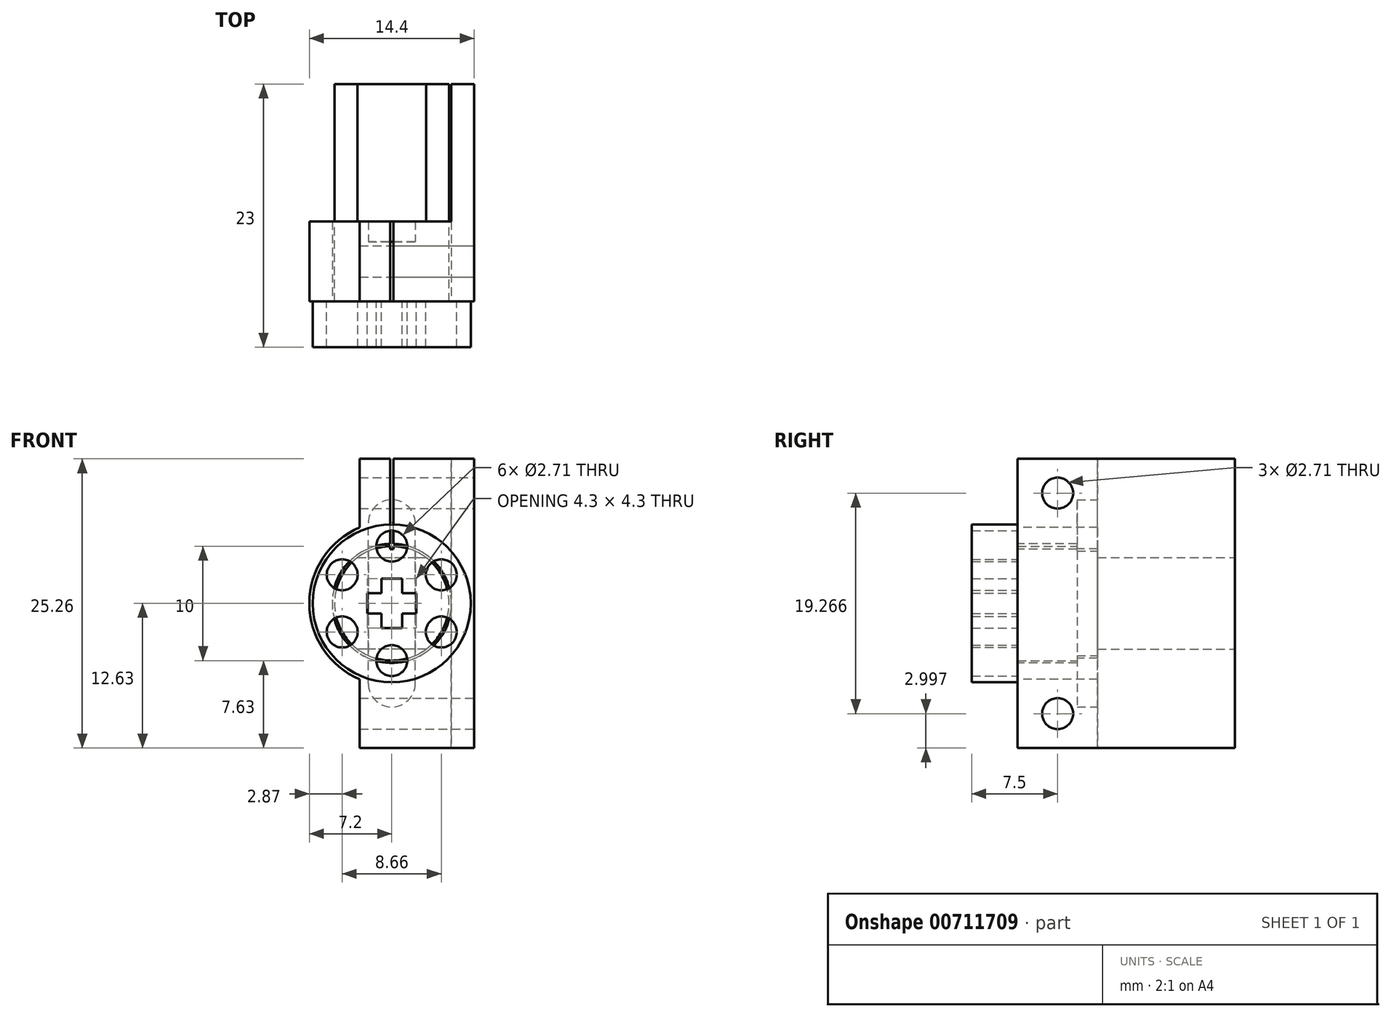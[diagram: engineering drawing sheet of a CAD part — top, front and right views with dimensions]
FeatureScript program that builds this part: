
annotation { "Feature Type Name" : "Feature", "Feature Type Description" : "" }
export const myFeature = defineFeature(function(context is Context, id is Id, definition is map)
    precondition{}
    {
        {
            var Q0;
            Q0=qCreatedBy(makeId("Front.planeOp"),FACE);
            var sketch = newSketch(context, id + "F0", { "sketchPlane" : qUnion([Q0])});
            skArc(sketch, "E0", {"start": v(-3, 4) * mm, "mid": v(-5, 0) * mm, "end": v(-3, -4) * mm});
            skLineSegment(sketch, "E1", {"start": v(-3, 4) * mm, "end": v(3, 4) * mm});
            skLineSegment(sketch, "E2", {"start": v(3, -4) * mm, "end": v(-3, -4) * mm});
            skArc(sketch, "E3.trimOffspring", {"start": v(3, -4) * mm, "mid": v(5, 0) * mm, "end": v(3, 4) * mm});
            skSolve(sketch);
        }
        {
            var Q0;
            Q0 = qSketchRegion(id + "F0", true);
            extrude(context, id + "F1", {"entities" : qUnion([Q0]), "depth" : 12 * mm, "offsetDistance" : 25.4 * mm});
        }
        {
            var Q0;
            Q0=makeQuery(id+"F1.opExtrude","CAP_FACE",FACE,{"disambiguationData":[OSD([sQuery(id+"F0.wireOp",EDGE,"E0"),sQuery(id+"F0.wireOp",EDGE,"E1"),sQuery(id+"F0.wireOp",EDGE,"E2"),sQuery(id+"F0.wireOp",EDGE,"E3.trimOffspring")])],"isStart":false});
            var sketch = newSketch(context, id + "F2", { "sketchPlane" : qUnion([Q0])});
            skCircle(sketch, "E4", {"center": v(0, 0) * mm, "radius": 5 * mm});
            skSolve(sketch);
        }
        {
            var Q0;
            Q0 = qSketchRegion(id + "F2", true);
            extrude(context, id + "F3", {"entities" : qUnion([Q0]), "operationType" : NewBodyOperationType.ADD, "depth" : 7 * mm, "offsetDistance" : 25 * mm});
        }
        {
            var Q0;
            Q0=makeQuery(id+"F3.opExtrude","CAP_FACE",FACE,{"disambiguationData":[OSD([sQuery(id+"F2.wireOp",EDGE,"E4")])],"isStart":false});
            var sketch = newSketch(context, id + "F4", { "sketchPlane" : qUnion([Q0])});
            skLineSegment(sketch, "E5.bottom", {"start": v(-0.75, 2) * mm, "end": v(0.75, 2) * mm});
            skLineSegment(sketch, "E5.top", {"start": v(-0.75, -2) * mm, "end": v(0.75, -2) * mm});
            skLineSegment(sketch, "E5.left", {"start": v(-0.75, 2) * mm, "end": v(-0.75, 0.75) * mm});
            skLineSegment(sketch, "E5.right", {"start": v(0.75, 2) * mm, "end": v(0.75, 0.75) * mm});
            skPoint(sketch, "E5.middle", {"position": v(0, 0) * mm});
            skLineSegment(sketch, "E6.bottom", {"start": v(-2, 0.75) * mm, "end": v(-0.75, 0.75) * mm});
            skLineSegment(sketch, "E6.top", {"start": v(-2, -0.75) * mm, "end": v(-0.75, -0.75) * mm});
            skLineSegment(sketch, "E6.left", {"start": v(-2, 0.75) * mm, "end": v(-2, -0.75) * mm});
            skLineSegment(sketch, "E6.right", {"start": v(2, 0.75) * mm, "end": v(2, -0.75) * mm});
            skLineSegment(sketch, "E7.trimOffspring", {"start": v(0.75, -0.75) * mm, "end": v(2, -0.75) * mm});
            skLineSegment(sketch, "E8.trimOffspring", {"start": v(-0.75, -0.75) * mm, "end": v(-0.75, -2) * mm});
            skLineSegment(sketch, "E9.trimOffspring", {"start": v(0.75, 0.75) * mm, "end": v(2, 0.75) * mm});
            skLineSegment(sketch, "E10.trimOffspring", {"start": v(0.75, -0.75) * mm, "end": v(0.75, -2) * mm});
            skSolve(sketch);
        }
        {
            var Q0;
            Q0 = qSketchRegion(id + "F4", true);
            extrude(context, id + "F5", {"entities" : qUnion([Q0]), "operationType" : NewBodyOperationType.ADD, "depth" : 2 * mm, "offsetDistance" : 25 * mm});
        }
        {
            var Q0;
            Q0=makeQuery(id+"F5.opExtrude","CAP_FACE",FACE,{"disambiguationData":[OSD([sQuery(id+"F4.wireOp",EDGE,"E5.bottom"),sQuery(id+"F4.wireOp",EDGE,"E5.top"),sQuery(id+"F4.wireOp",EDGE,"E5.left"),sQuery(id+"F4.wireOp",EDGE,"E5.right"),sQuery(id+"F4.wireOp",EDGE,"E6.bottom"),sQuery(id+"F4.wireOp",EDGE,"E6.top"),sQuery(id+"F4.wireOp",EDGE,"E6.left"),sQuery(id+"F4.wireOp",EDGE,"E6.right"),sQuery(id+"F4.wireOp",EDGE,"E7.trimOffspring"),sQuery(id+"F4.wireOp",EDGE,"E8.trimOffspring"),sQuery(id+"F4.wireOp",EDGE,"E9.trimOffspring"),sQuery(id+"F4.wireOp",EDGE,"E10.trimOffspring")])],"isStart":false});
            var sketch = newSketch(context, id + "F6", { "sketchPlane" : qUnion([Q0])});
            skCircle(sketch, "E11", {"center": v(0, 0) * mm, "radius": 0.75 * mm});
            skSolve(sketch);
        }
        {
            var Q0;
            Q0 = qSketchRegion(id + "F6", true);
            extrude(context, id + "F7", {"entities" : qUnion([Q0]), "operationType" : NewBodyOperationType.ADD, "depth" : 1 * mm, "offsetDistance" : 25 * mm});
        }
        {
            var Q0;
            {var subQ0=sQuery(id+"F2.wireOp",EDGE,"E4");Q0=makeQuery(id+"F3.boolean.opBoolean","SPLIT",FACE,{"disambiguationData":[TD([makeQuery(id+"F1.opExtrude","SWEPT_FACE",FACE,{"disambiguationData":[OSD([sQuery(id+"F0.wireOp",EDGE,"E1")])]})])],"derivedFrom":makeQuery(id+"F3.opExtrude","CAP_FACE",FACE,{"disambiguationData":[OSD([subQ0])],"isStart":true})});}
            var sketch = newSketch(context, id + "F8", { "sketchPlane" : qUnion([Q0])});
            skLineSegment(sketch, "E12", {"start": v(0, 0) * mm, "end": v(0, 7) * mm, "construction": true});
            skPoint(sketch, "E12.endSnap0", {"position": v(0, 5) * mm});
            skCircle(sketch, "E13", {"center": v(0, 7) * mm, "radius": 1 * mm});
            skLineSegment(sketch, "E14", {"start": v(-1.9, 4) * mm, "end": v(-1.9, 7) * mm});
            skArc(sketch, "E15", {"start": v(-1.9, 7) * mm, "mid": v(0, 8.9) * mm, "end": v(1.9, 7) * mm});
            skLineSegment(sketch, "E16", {"start": v(1.9, 7) * mm, "end": v(1.9, 4) * mm});
            skLineSegment(sketch, "E17", {"start": v(1.9, 4) * mm, "end": v(-1.9, 4) * mm});
            skLineSegment(sketch, "E18", {"start": v(0, 0) * mm, "end": v(-2.98, 0) * mm, "construction": true});
            skPoint(sketch, "E19.MirrorP", {"position": v(0, -5) * mm});
            skLineSegment(sketch, "E20.MirrorCS", {"start": v(0, 0) * mm, "end": v(0, -7) * mm, "construction": true});
            skCircle(sketch, "E21.MirrorC", {"center": v(0, -7) * mm, "radius": 1 * mm});
            skLineSegment(sketch, "E22.MirrorCS", {"start": v(-1.9, -4) * mm, "end": v(-1.9, -7) * mm});
            skLineSegment(sketch, "E23.MirrorCS", {"start": v(1.9, -7) * mm, "end": v(1.9, -4) * mm});
            skLineSegment(sketch, "E24.MirrorCS", {"start": v(1.9, -4) * mm, "end": v(-1.9, -4) * mm});
            skArc(sketch, "E25.MirrorCS", {"start": v(-1.9, -7) * mm, "mid": v(0, -8.9) * mm, "end": v(1.9, -7) * mm});
            skSolve(sketch);
        }
        {
            var Q0;
            Q0 = qSketchRegion(id + "F8", true);
            extrude(context, id + "F9", {"entities" : qUnion([Q0]), "operationType" : NewBodyOperationType.ADD, "oppositeDirection" : true, "depth" : 1.8 * mm, "offsetDistance" : 25 * mm});
        }
        {
            var Q0;
            Q0=makeQuery(id+"F1.opExtrude","SWEPT_BODY",BODY,{"disambiguationData":[OSD([sQuery(id+"F0.wireOp",EDGE,"E0"),sQuery(id+"F0.wireOp",EDGE,"E1"),sQuery(id+"F0.wireOp",EDGE,"E2"),sQuery(id+"F0.wireOp",EDGE,"E3.trimOffspring")])]});
            transform(context, id + "F10", {"entities" : qUnion([Q0]), "transformType" : TransformType.TRANSLATION_3D, "dx" : 0 * mm, "dy" : 0 * mm, "dz" : 0 * mm, "makeCopy" : true});
        }
        {
            var Q0;
            Q0=makeQuery(id+"F10.opPattern","COPY",BODY,{"derivedFrom":makeQuery(id+"F1.opExtrude","SWEPT_BODY",BODY,{"disambiguationData":[OSD([sQuery(id+"F0.wireOp",EDGE,"E0"),sQuery(id+"F0.wireOp",EDGE,"E1"),sQuery(id+"F0.wireOp",EDGE,"E2"),sQuery(id+"F0.wireOp",EDGE,"E3.trimOffspring")])]}),"instanceName":"1"});
            deleteBodies(context, id + "F11", {"entities" : qUnion([Q0])});
        }
        {
            var Q0;
            Q0=makeQuery(id+"F3.opExtrude","CAP_FACE",FACE,{"disambiguationData":[OSD([sQuery(id+"F2.wireOp",EDGE,"E4")])],"isStart":false});
            var sketch = newSketch(context, id + "F12", { "sketchPlane" : qUnion([Q0])});
            skCircle(sketch, "E26.0", {"center": v(0, 0) * mm, "radius": 5.2 * mm});
            skLineSegment(sketch, "E27", {"start": v(7.2, 0) * mm, "end": v(7.2, 12.63) * mm});
            skLineSegment(sketch, "E28", {"start": v(7.2, 12.63) * mm, "end": v(-2.8, 12.63) * mm});
            skLineSegment(sketch, "E29", {"start": v(-2.8, 12.63) * mm, "end": v(-2.8, 6.63) * mm});
            skArc(sketch, "E30", {"start": v(-2.8, 6.63) * mm, "mid": v(-7.2, 0) * mm, "end": v(-2.8, -6.63) * mm});
            skLineSegment(sketch, "E31", {"start": v(0, 7.2) * mm, "end": v(0, 0) * mm, "construction": true});
            skLineSegment(sketch, "E32", {"start": v(7.2, 0) * mm, "end": v(7.2, -12.63) * mm});
            skLineSegment(sketch, "E33", {"start": v(7.2, -12.63) * mm, "end": v(-2.8, -12.63) * mm});
            skLineSegment(sketch, "E34", {"start": v(-2.8, -12.63) * mm, "end": v(-2.8, -6.63) * mm});
            skSolve(sketch);
        }
        {
            var Q0;
            Q0=makeQuery(id+"F12.imprint","IMPRINT",FACE,{"disambiguationData":[TD([[makeQuery(id+"F12.imprint","IMPRINT",EDGE,{"derivedFrom":sQuery(id+"F12.wireOp",EDGE,"E26.0")}),-1.0]])]});
            var Q1;
            {var subQ0=sQuery(id+"F2.wireOp",EDGE,"E4");Q1=makeQuery(id+"F9.boolean.opBoolean","MERGE",FACE,{"derivedFrom":[makeQuery(id+"F3.boolean.opBoolean","SPLIT",FACE,{"disambiguationData":[TD([makeQuery(id+"F1.opExtrude","SWEPT_FACE",FACE,{"disambiguationData":[OSD([sQuery(id+"F0.wireOp",EDGE,"E2")])]})])],"derivedFrom":makeQuery(id+"F3.opExtrude","CAP_FACE",FACE,{"disambiguationData":[OSD([subQ0])],"isStart":true})}),makeQuery(id+"F9.opExtrude","CAP_FACE",FACE,{"disambiguationData":[OSD([sQuery(id+"F8.wireOp",EDGE,"E21.MirrorC"),sQuery(id+"F8.wireOp",EDGE,"E22.MirrorCS"),sQuery(id+"F8.wireOp",EDGE,"E23.MirrorCS"),sQuery(id+"F8.wireOp",EDGE,"E24.MirrorCS"),sQuery(id+"F8.wireOp",EDGE,"E25.MirrorCS")])],"isStart":true})]});}
            extrude(context, id + "F13", {"entities" : qUnion([Q0]), "endBound" : BoundingType.UP_TO_SURFACE, "oppositeDirection" : true, "depth" : 25 * mm, "endBoundEntityFace" : qUnion([Q1]), "offsetDistance" : 25 * mm});
        }
        {
            var Q0;
            Q0=makeQuery(id+"F13.opExtrude","CAP_FACE",FACE,{"disambiguationData":[OSD([sQuery(id+"F12.wireOp",EDGE,"E26.0"),sQuery(id+"F12.wireOp",EDGE,"E27"),sQuery(id+"F12.wireOp",EDGE,"E28"),sQuery(id+"F12.wireOp",EDGE,"E29"),sQuery(id+"F12.wireOp",EDGE,"E30"),sQuery(id+"F12.wireOp",EDGE,"E32"),sQuery(id+"F12.wireOp",EDGE,"E33"),sQuery(id+"F12.wireOp",EDGE,"E34")])],"isStart":false});
            var sketch = newSketch(context, id + "F14", { "sketchPlane" : qUnion([Q0])});
            skArc(sketch, "E35.0", {"start": v(-2.05, -7) * mm, "mid": v(0, -9.05) * mm, "end": v(2.05, -7) * mm});
            skLineSegment(sketch, "E36", {"start": v(2.05, -7) * mm, "end": v(2.05, 4.78) * mm});
            skLineSegment(sketch, "E37", {"start": v(-2.05, -7) * mm, "end": v(-2.05, 4.78) * mm});
            skLineSegment(sketch, "E38.0", {"start": v(2.05, 7) * mm, "end": v(2.05, 4.65) * mm});
            skArc(sketch, "E38.1", {"start": v(-2.05, 7) * mm, "mid": v(0, 9.05) * mm, "end": v(2.05, 7) * mm});
            skLineSegment(sketch, "E38.2", {"start": v(-2.05, 4.62) * mm, "end": v(-2.05, 7) * mm});
            skSolve(sketch);
        }
        {
            var Q0;
            Q0 = qSketchRegion(id + "F14", true);
            var Q1;
            Q1=makeQuery(id+"F9.opExtrude","CAP_FACE",FACE,{"disambiguationData":[OSD([sQuery(id+"F8.wireOp",EDGE,"E13"),sQuery(id+"F8.wireOp",EDGE,"E14"),sQuery(id+"F8.wireOp",EDGE,"E15"),sQuery(id+"F8.wireOp",EDGE,"E16"),sQuery(id+"F8.wireOp",EDGE,"E17")])],"isStart":false});
            extrude(context, id + "F15", {"entities" : qUnion([Q0]), "operationType" : NewBodyOperationType.REMOVE, "endBound" : BoundingType.UP_TO_SURFACE, "oppositeDirection" : true, "depth" : 25 * mm, "endBoundEntityFace" : qUnion([Q1]), "offsetDistance" : 25 * mm});
        }
        {
            var Q0;
            Q0=makeQuery(id+"F13.opExtrude","SWEPT_FACE",FACE,{"disambiguationData":[OSD([sQuery(id+"F12.wireOp",EDGE,"E34")])]});
            var sketch = newSketch(context, id + "F16", { "sketchPlane" : qUnion([Q0])});
            skPoint(sketch, "E39", {"position": v(15.5, -9.63) * mm});
            skPoint(sketch, "E39.positionSnap0", {"position": v(19, -9.63) * mm});
            skPoint(sketch, "E39.positionSnap1", {"position": v(15.5, -12.63) * mm});
            skPoint(sketch, "E40", {"position": v(15.5, 9.63) * mm});
            skSolve(sketch);
        }
        {
            var Q0;
            Q0=sQuery(id+"F16.wireOp",VERTEX,"E39");
            var Q1;
            Q1=sQuery(id+"F16.wireOp",VERTEX,"E40");
            var Q2;
            Q2=makeQuery(id+"F13.opExtrude","SWEPT_BODY",BODY,{"disambiguationData":[OSD([sQuery(id+"F12.wireOp",EDGE,"E26.0"),sQuery(id+"F12.wireOp",EDGE,"E27"),sQuery(id+"F12.wireOp",EDGE,"E28"),sQuery(id+"F12.wireOp",EDGE,"E29"),sQuery(id+"F12.wireOp",EDGE,"E30"),sQuery(id+"F12.wireOp",EDGE,"E32"),sQuery(id+"F12.wireOp",EDGE,"E33"),sQuery(id+"F12.wireOp",EDGE,"E34")])]});
            hole(context, id + "F17", {"style" : HoleStyle.SIMPLE, "endStyle" : HoleEndStyle.THROUGH, "standardTappedOrClearance" : lookupTablePath({ "standard" : "ANSI", "engagement" : "75%", "pitch" : "32 tpi", "size" : "#6", "type" : "Tapped" }), "standardBlindInLast" : lookupTablePath({ "fit" : "Free", "standard" : "ANSI", "engagement" : "75%", "pitch" : "32 tpi", "size" : "#6", "type" : "Clearance & tapped" }), "holeDiameter" : 2.7 * mm, "majorDiameter" : 3.5 * mm, "showTappedDepth" : true, "tappedDepth" : 5 * mm, "tapClearance" : 3, "locations" : qUnion([Q0, Q1]), "scope" : qUnion([Q2]), "startStyle" : HoleStartStyle.SKETCH});
        }
        {
            var Q0;
            Q0=makeQuery(id+"F13.opExtrude","CAP_FACE",FACE,{"disambiguationData":[OSD([sQuery(id+"F12.wireOp",EDGE,"E26.0"),sQuery(id+"F12.wireOp",EDGE,"E27"),sQuery(id+"F12.wireOp",EDGE,"E28"),sQuery(id+"F12.wireOp",EDGE,"E29"),sQuery(id+"F12.wireOp",EDGE,"E30"),sQuery(id+"F12.wireOp",EDGE,"E32"),sQuery(id+"F12.wireOp",EDGE,"E33"),sQuery(id+"F12.wireOp",EDGE,"E34")])],"isStart":true});
            var sketch = newSketch(context, id + "F18", { "sketchPlane" : qUnion([Q0])});
            skLineSegment(sketch, "E41", {"start": v(0, 5.2) * mm, "end": v(0, 12.63) * mm, "construction": true});
            skLineSegment(sketch, "E42.bottom", {"start": v(-0.15, 4.73) * mm, "end": v(0.15, 4.73) * mm});
            skLineSegment(sketch, "E42.top", {"start": v(-0.15, 13.1) * mm, "end": v(0.15, 13.1) * mm});
            skLineSegment(sketch, "E42.left", {"start": v(-0.15, 4.73) * mm, "end": v(-0.15, 13.1) * mm});
            skLineSegment(sketch, "E42.right", {"start": v(0.15, 4.73) * mm, "end": v(0.15, 13.1) * mm});
            skPoint(sketch, "E42.middle", {"position": v(0, 8.92) * mm});
            skSolve(sketch);
        }
        {
            var Q0;
            Q0 = qSketchRegion(id + "F18", true);
            var Q1;
            Q1=makeQuery(id+"F13.opExtrude","CAP_FACE",FACE,{"disambiguationData":[OSD([sQuery(id+"F12.wireOp",EDGE,"E26.0"),sQuery(id+"F12.wireOp",EDGE,"E27"),sQuery(id+"F12.wireOp",EDGE,"E28"),sQuery(id+"F12.wireOp",EDGE,"E29"),sQuery(id+"F12.wireOp",EDGE,"E30"),sQuery(id+"F12.wireOp",EDGE,"E32"),sQuery(id+"F12.wireOp",EDGE,"E33"),sQuery(id+"F12.wireOp",EDGE,"E34")])],"isStart":false});
            extrude(context, id + "F19", {"entities" : qUnion([Q0]), "operationType" : NewBodyOperationType.REMOVE, "endBound" : BoundingType.UP_TO_SURFACE, "oppositeDirection" : true, "depth" : 25 * mm, "endBoundEntityFace" : qUnion([Q1]), "offsetDistance" : 25 * mm});
        }
        {
            var Q0;
            Q0=makeQuery(id+"F13.opExtrude","CAP_FACE",FACE,{"disambiguationData":[OSD([sQuery(id+"F12.wireOp",EDGE,"E26.0"),sQuery(id+"F12.wireOp",EDGE,"E27"),sQuery(id+"F12.wireOp",EDGE,"E28"),sQuery(id+"F12.wireOp",EDGE,"E29"),sQuery(id+"F12.wireOp",EDGE,"E30"),sQuery(id+"F12.wireOp",EDGE,"E32"),sQuery(id+"F12.wireOp",EDGE,"E33"),sQuery(id+"F12.wireOp",EDGE,"E34")])],"isStart":false});
            var sketch = newSketch(context, id + "F20", { "sketchPlane" : qUnion([Q0])});
            skLineSegment(sketch, "E43.bottom", {"start": v(-7.2, -12.63) * mm, "end": v(-5.2, -12.63) * mm});
            skLineSegment(sketch, "E43.top", {"start": v(-7.2, 12.63) * mm, "end": v(-5.2, 12.63) * mm});
            skLineSegment(sketch, "E43.left", {"start": v(-7.2, -12.63) * mm, "end": v(-7.2, 12.63) * mm});
            skLineSegment(sketch, "E43.right", {"start": v(-5.2, -12.63) * mm, "end": v(-5.2, 12.63) * mm});
            skSolve(sketch);
        }
        {
            var Q0;
            Q0 = qSketchRegion(id + "F20", true);
            var Q1;
            Q1=makeQuery(id+"F1.opExtrude","CAP_FACE",FACE,{"disambiguationData":[OSD([sQuery(id+"F0.wireOp",EDGE,"E0"),sQuery(id+"F0.wireOp",EDGE,"E1"),sQuery(id+"F0.wireOp",EDGE,"E2"),sQuery(id+"F0.wireOp",EDGE,"E3.trimOffspring")])],"isStart":true});
            extrude(context, id + "F21", {"entities" : qUnion([Q0]), "operationType" : NewBodyOperationType.ADD, "endBound" : BoundingType.UP_TO_SURFACE, "depth" : 25 * mm, "endBoundEntityFace" : qUnion([Q1]), "offsetDistance" : 25 * mm});
        }
        {
            var Q0;
            Q0=makeQuery(id+"F3.opExtrude","CAP_FACE",FACE,{"disambiguationData":[OSD([sQuery(id+"F2.wireOp",EDGE,"E4")])],"isStart":false});
            var sketch = newSketch(context, id + "F22", { "sketchPlane" : qUnion([Q0])});
            skLineSegment(sketch, "E44.0", {"start": v(-2.15, 0.9) * mm, "end": v(-2.15, -0.9) * mm});
            skLineSegment(sketch, "E44.1", {"start": v(0.9, 0.9) * mm, "end": v(2.15, 0.9) * mm});
            skLineSegment(sketch, "E44.2", {"start": v(0.9, 2.15) * mm, "end": v(0.9, 0.9) * mm});
            skLineSegment(sketch, "E44.3", {"start": v(-0.9, 2.15) * mm, "end": v(0.9, 2.15) * mm});
            skLineSegment(sketch, "E44.4", {"start": v(-0.9, 2.15) * mm, "end": v(-0.9, 0.9) * mm});
            skLineSegment(sketch, "E44.5", {"start": v(2.15, 0.9) * mm, "end": v(2.15, -0.9) * mm});
            skLineSegment(sketch, "E44.6", {"start": v(-2.15, 0.9) * mm, "end": v(-0.9, 0.9) * mm});
            skLineSegment(sketch, "E44.7", {"start": v(0.9, -0.9) * mm, "end": v(2.15, -0.9) * mm});
            skLineSegment(sketch, "E44.8", {"start": v(0.9, -0.9) * mm, "end": v(0.9, -2.15) * mm});
            skLineSegment(sketch, "E44.9", {"start": v(-0.9, -2.15) * mm, "end": v(0.9, -2.15) * mm});
            skLineSegment(sketch, "E44.10", {"start": v(-0.9, -0.9) * mm, "end": v(-0.9, -2.15) * mm});
            skLineSegment(sketch, "E44.11", {"start": v(-2.15, -0.9) * mm, "end": v(-0.9, -0.9) * mm});
            skSolve(sketch);
        }
        {
            var Q0;
            Q0=makeQuery(id+"F22.imprint","IMPRINT",FACE,{"disambiguationData":[TD([[makeQuery(id+"F22.imprint","IMPRINT",EDGE,{"derivedFrom":sQuery(id+"F22.wireOp",EDGE,"E44.0")}),-1.0]])]});
            var sketch = newSketch(context, id + "F23", { "sketchPlane" : qUnion([Q0])});
            skCircle(sketch, "E45", {"center": v(0, 0) * mm, "radius": 6.9 * mm});
            skSolve(sketch);
        }
        {
            var Q0;
            Q0 = qSketchRegion(id + "F23", true);
            extrude(context, id + "F24", {"entities" : qUnion([Q0]), "depth" : 4 * mm, "offsetDistance" : 25 * mm});
        }
        {
            var Q0;
            Q0 = qSketchRegion(id + "F22", true);
            var Q1;
            Q1=makeQuery(id+"F24.opExtrude","CAP_FACE",FACE,{"disambiguationData":[OSD([sQuery(id+"F23.wireOp",EDGE,"E45")])],"isStart":false});
            extrude(context, id + "F25", {"entities" : qUnion([Q0]), "operationType" : NewBodyOperationType.REMOVE, "endBound" : BoundingType.UP_TO_SURFACE, "depth" : 25 * mm, "endBoundEntityFace" : qUnion([Q1]), "offsetDistance" : 25 * mm});
        }
        {
            var Q0;
            Q0=makeQuery(id+"F24.opExtrude","CAP_FACE",FACE,{"disambiguationData":[OSD([sQuery(id+"F23.wireOp",EDGE,"E45")])],"isStart":false});
            var sketch = newSketch(context, id + "F26", { "sketchPlane" : qUnion([Q0])});
            skPoint(sketch, "E46", {"position": v(0, 5) * mm});
            skPoint(sketch, "E47.1.0", {"position": v(-4.33, 2.5) * mm});
            skPoint(sketch, "E47.2.0", {"position": v(-4.33, -2.5) * mm});
            skPoint(sketch, "E47.3.0", {"position": v(0, -5) * mm});
            skPoint(sketch, "E47.4.0", {"position": v(4.33, -2.5) * mm});
            skPoint(sketch, "E47.5.0", {"position": v(4.33, 2.5) * mm});
            skPoint(sketch, "E47.center", {"position": v(0, 0) * mm});
            skSolve(sketch);
        }
        {
            var Q0;
            Q0=sQuery(id+"F26.wireOp",VERTEX,"E47.2.0");
            var Q1;
            Q1=sQuery(id+"F26.wireOp",VERTEX,"E47.1.0");
            var Q2;
            Q2=sQuery(id+"F26.wireOp",VERTEX,"E46");
            var Q3;
            Q3=sQuery(id+"F26.wireOp",VERTEX,"E47.5.0");
            var Q4;
            Q4=sQuery(id+"F26.wireOp",VERTEX,"E47.4.0");
            var Q5;
            Q5=sQuery(id+"F26.wireOp",VERTEX,"E47.3.0");
            var Q6;
            Q6=makeQuery(id+"F24.opExtrude","SWEPT_BODY",BODY,{"disambiguationData":[OSD([sQuery(id+"F23.wireOp",EDGE,"E45")])]});
            hole(context, id + "F27", {"style" : HoleStyle.SIMPLE, "endStyle" : HoleEndStyle.THROUGH, "standardTappedOrClearance" : lookupTablePath({ "standard" : "ANSI", "engagement" : "75%", "pitch" : "32 tpi", "size" : "#6", "type" : "Tapped" }), "standardBlindInLast" : lookupTablePath({ "fit" : "Free", "standard" : "ANSI", "engagement" : "75%", "pitch" : "32 tpi", "size" : "#6", "type" : "Clearance & tapped" }), "holeDiameter" : 2.7 * mm, "majorDiameter" : 3.5 * mm, "showTappedDepth" : true, "tappedDepth" : 3 * mm, "tapClearance" : 3, "locations" : qUnion([Q0, Q1, Q2, Q3, Q4, Q5]), "scope" : qUnion([Q6]), "startStyle" : HoleStartStyle.SKETCH});
        }
    });
